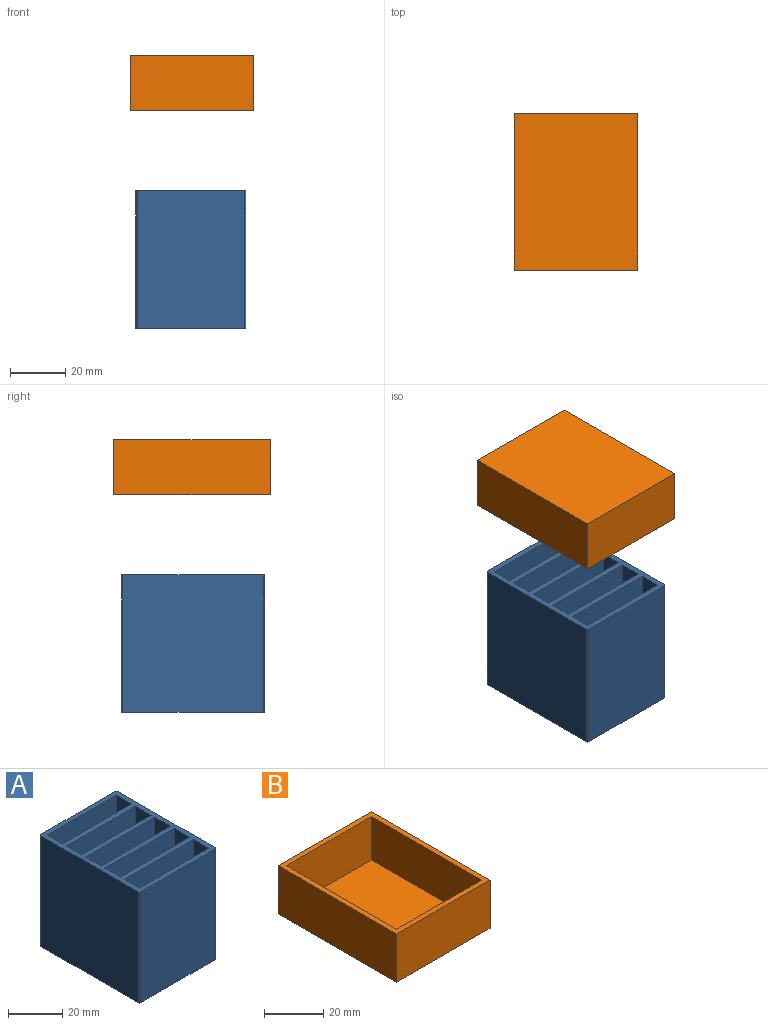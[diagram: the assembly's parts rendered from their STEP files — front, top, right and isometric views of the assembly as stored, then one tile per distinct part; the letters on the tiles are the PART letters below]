
ASSEMBLY  parts=2 mates=2
PART A: 35 faces, bbox 40x52x50 mm
  f0: plane 51x50mm, normal (1,0,0), area 2550mm2, adj f1,f7,f8,f29
  f1: cylinder r=0.5mm len=50mm, axis (0,0,-1), area 39.3mm2, adj f0,f2,f8,f29
  f2: plane 50x39mm, normal (0,1,0), area 1950mm2, adj f1,f3,f8,f29
  f3: cylinder r=0.5mm len=50mm, axis (0,0,-1), area 39.3mm2, adj f2,f4,f8,f29
  f4: plane 51x50mm, normal (-1,0,0), area 2550mm2, adj f3,f5,f8,f29
  f5: cylinder r=0.5mm len=50mm, axis (0,0,-1), area 39.3mm2, adj f4,f6,f8,f29
  f6: plane 50x39mm, normal (0,-1,0), area 1950mm2, adj f5,f7,f8,f29
  f7: cylinder r=0.5mm len=50mm, axis (0,0,-1), area 39.3mm2, adj f0,f6,f8,f29
  f8: plane 52x40mm, normal (0,0,-1), area 2079.8mm2, adj f0,f1,f2,f3,f4,f5,f6,f7
  f9: plane 48x8mm, normal (1,0,0), area 384mm2, adj f10,f24,f29,f34
  f10: plane 48x36mm, normal (0,-1,0), area 1728mm2, adj f9,f11,f29,f34
  f11: plane 48x8mm, normal (-1,0,0), area 384mm2, adj f10,f24,f29,f34
  f12: plane 48x8mm, normal (1,0,0), area 384mm2, adj f13,f25,f29,f33
  f13: plane 48x36mm, normal (0,-1,0), area 1728mm2, adj f12,f14,f29,f33
  f14: plane 48x8mm, normal (-1,0,0), area 384mm2, adj f13,f25,f29,f33
  f15: plane 48x8mm, normal (1,0,0), area 384mm2, adj f16,f26,f29,f32
  f16: plane 48x36mm, normal (0,-1,0), area 1728mm2, adj f15,f17,f29,f32
  f17: plane 48x8mm, normal (-1,0,0), area 384mm2, adj f16,f26,f29,f32
  f18: plane 48x8mm, normal (1,0,0), area 384mm2, adj f19,f27,f29,f31
  f19: plane 48x36mm, normal (0,-1,0), area 1728mm2, adj f18,f20,f29,f31
  f20: plane 48x8mm, normal (-1,0,0), area 384mm2, adj f19,f27,f29,f31
  f21: plane 48x8mm, normal (1,0,0), area 384mm2, adj f22,f28,f29,f30
  f22: plane 48x36mm, normal (0,-1,0), area 1728mm2, adj f21,f23,f29,f30
  f23: plane 48x8mm, normal (-1,0,0), area 384mm2, adj f22,f28,f29,f30
  f24: plane 48x36mm, normal (0,1,0), area 1728mm2, adj f9,f11,f29,f34
  f25: plane 48x36mm, normal (0,1,0), area 1728mm2, adj f12,f14,f29,f33
  f26: plane 48x36mm, normal (0,1,0), area 1728mm2, adj f15,f17,f29,f32
  f27: plane 48x36mm, normal (0,1,0), area 1728mm2, adj f18,f20,f29,f31
  f28: plane 48x36mm, normal (0,1,0), area 1728mm2, adj f21,f23,f29,f30
  f29: plane 52x40mm, normal (0,0,1), area 639.8mm2, adj f0,f1,f2,f3,f4,f5,f6,f7
  f30: plane 36x8mm, normal (0,0,1), area 288mm2, adj f21,f22,f23,f28
  f31: plane 36x8mm, normal (0,0,1), area 288mm2, adj f18,f19,f20,f27
  f32: plane 36x8mm, normal (0,0,1), area 288mm2, adj f15,f16,f17,f26
  f33: plane 36x8mm, normal (0,0,1), area 288mm2, adj f12,f13,f14,f25
  f34: plane 36x8mm, normal (0,0,1), area 288mm2, adj f9,f10,f11,f24
PART B: 11 faces, bbox 44.8x56.8x20 mm
  f0: plane 44.75x20mm, normal (0,1,0), area 895mm2, adj f1,f3,f4,f9
  f1: plane 56.75x20mm, normal (-1,0,0), area 1135mm2, adj f0,f2,f4,f9
  f2: plane 44.75x20mm, normal (0,-1,0), area 895mm2, adj f1,f3,f4,f9
  f3: plane 56.75x20mm, normal (1,0,0), area 1135mm2, adj f0,f2,f4,f9
  f4: plane 56.75x44.75mm, normal (0,0,-1), area 2539.6mm2, adj f0,f1,f2,f3
  f5: plane 52.75x18mm, normal (1,0,0), area 949.5mm2, adj f6,f8,f9,f10
  f6: plane 40.75x18mm, normal (0,-1,0), area 733.5mm2, adj f5,f7,f9,f10
  f7: plane 52.75x18mm, normal (-1,0,0), area 949.5mm2, adj f6,f8,f9,f10
  f8: plane 40.75x18mm, normal (0,1,0), area 733.5mm2, adj f5,f7,f9,f10
  f9: plane 56.75x44.75mm, normal (0,0,1), area 390mm2, adj f0,f1,f2,f3,f5,f6,f7,f8
  f10: plane 52.75x40.75mm, normal (0,0,1), area 2149.6mm2, adj f5,f6,f7,f8
PLACE A t=(-128.85,5.09,42.9)mm
PLACE B rot(axis=(0,-1,0),180deg) t=(-213.36,4.54,142.1)mm
MATE planar B.f7 <-> A.f4  axis (1,0,0) through (-191.62,58.66,131.1)mm
MATE planar B.f8 <-> A.f6  axis (0,1,0) through (-171.25,32.29,131.1)mm
